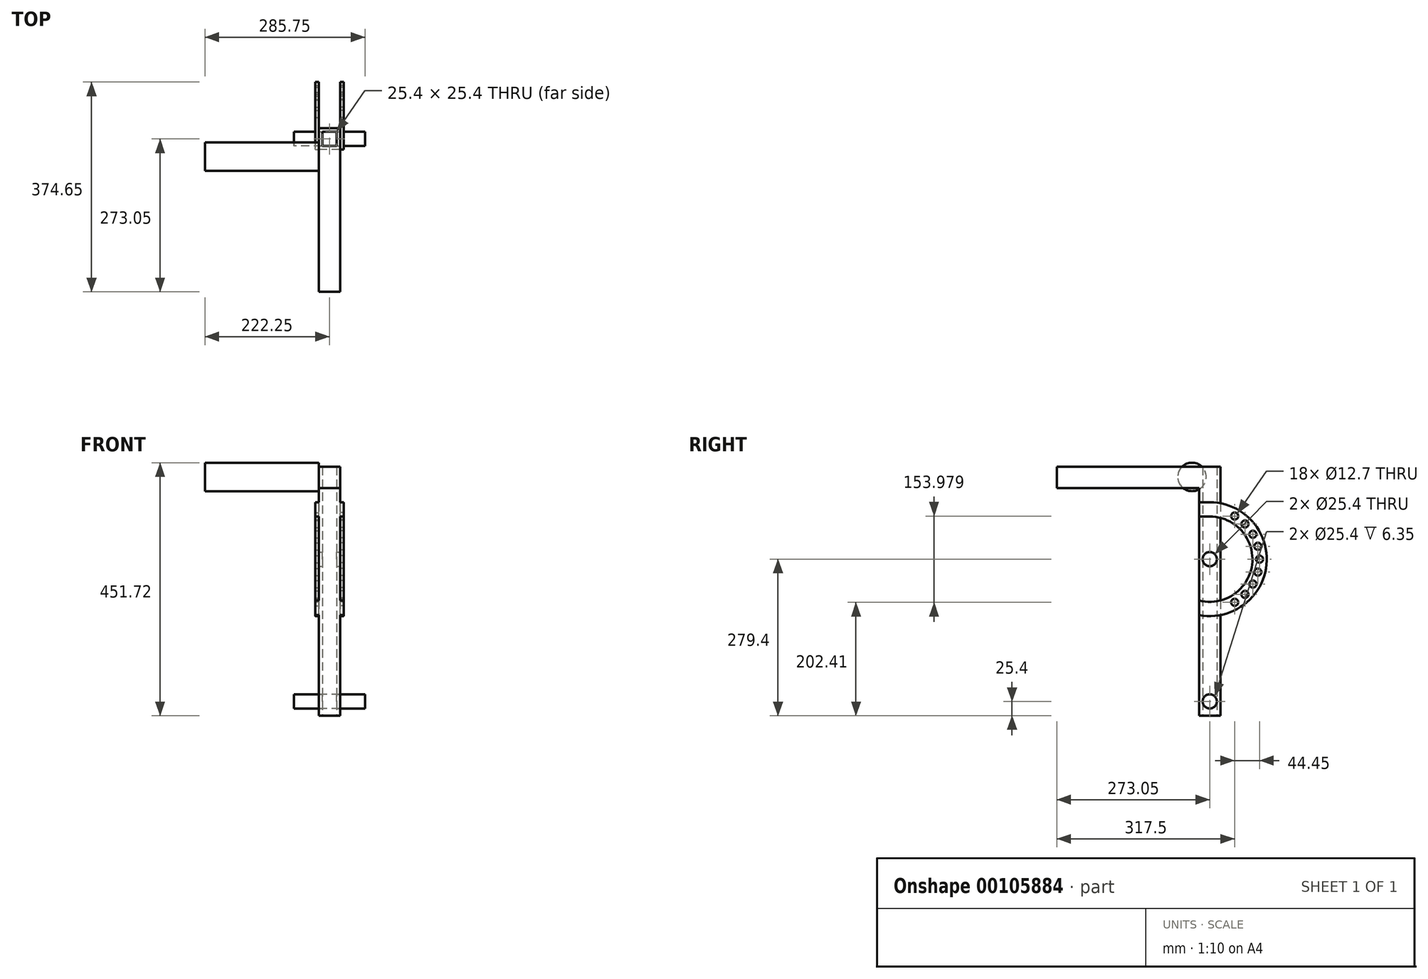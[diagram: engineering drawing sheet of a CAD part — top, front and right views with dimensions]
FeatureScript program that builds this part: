
annotation { "Feature Type Name" : "Feature", "Feature Type Description" : "" }
export const myFeature = defineFeature(function(context is Context, id is Id, definition is map)
    precondition{}
    {
        {
            var Q0;
            Q0=qCreatedBy(makeId("Top.planeOp"),FACE);
            var sketch = newSketch(context, id + "F0", { "sketchPlane" : qUnion([Q0])});
            skLineSegment(sketch, "E0.bottom", {"start": v(19.05, 19.05) * mm, "end": v(-19.05, 19.05) * mm});
            skLineSegment(sketch, "E0.top", {"start": v(19.05, -19.05) * mm, "end": v(-19.05, -19.05) * mm});
            skLineSegment(sketch, "E0.left", {"start": v(19.05, 19.05) * mm, "end": v(19.05, -19.05) * mm});
            skLineSegment(sketch, "E0.right", {"start": v(-19.05, 19.05) * mm, "end": v(-19.05, -19.05) * mm});
            skPoint(sketch, "E0.middle", {"position": v(0, 0) * mm});
            skLineSegment(sketch, "E1.0", {"start": v(12.7, 12.7) * mm, "end": v(-12.7, 12.7) * mm});
            skLineSegment(sketch, "E1.1", {"start": v(12.7, 12.7) * mm, "end": v(12.7, -12.7) * mm});
            skLineSegment(sketch, "E1.2", {"start": v(12.7, -12.7) * mm, "end": v(-12.7, -12.7) * mm});
            skLineSegment(sketch, "E1.3", {"start": v(-12.7, 12.7) * mm, "end": v(-12.7, -12.7) * mm});
            skSolve(sketch);
        }
        {
            var Q0;
            Q0 = qSketchRegion(id + "F0", true);
            extrude(context, id + "F1", {"entities" : qUnion([Q0]), "depth" : 444.5 * mm});
        }
        {
            var Q0;
            Q0=makeQuery(id+"F1.opExtrude","SWEPT_FACE",FACE,{"disambiguationData":[OSD([sQuery(id+"F0.wireOp",EDGE,"E0.left")])]});
            var sketch = newSketch(context, id + "F2", { "sketchPlane" : qUnion([Q0])});
            skCircle(sketch, "E2", {"center": v(0, 25.4) * mm, "radius": 12.7 * mm});
            skLineSegment(sketch, "E3", {"start": v(-19.05, 222.25) * mm, "end": v(19.05, 222.25) * mm, "construction": true});
            skCircle(sketch, "E4", {"center": v(0, 279.4) * mm, "radius": 12.7 * mm});
            skSolve(sketch);
        }
        {
            var Q0;
            Q0 = qSketchRegion(id + "F2", true);
            var Q1;
            Q1=makeQuery(id+"F1.opExtrude","SWEPT_FACE",FACE,{"disambiguationData":[OSD([sQuery(id+"F0.wireOp",EDGE,"E0.right")])]});
            extrude(context, id + "F3", {"entities" : qUnion([Q0]), "operationType" : NewBodyOperationType.REMOVE, "endBound" : BoundingType.UP_TO_SURFACE, "oppositeDirection" : true, "endBoundEntityFace" : qUnion([Q1]), "depth" : 25.4 * mm});
        }
        {
            var Q0;
            Q0=qCreatedBy(makeId("Right.planeOp"),FACE);
            var sketch = newSketch(context, id + "F4", { "sketchPlane" : qUnion([Q0])});
            skCircle(sketch, "E5", {"center": v(0, 25.4) * mm, "radius": 12.7 * mm});
            skSolve(sketch);
        }
        {
            var Q0;
            Q0 = qSketchRegion(id + "F4", true);
            extrude(context, id + "F5", {"entities" : qUnion([Q0]), "endBound" : BoundingType.SYMMETRIC, "depth" : 127 * mm});
        }
        {
            var Q0;
            Q0=makeQuery(id+"F2.imprint","IMPRINT",FACE,{"disambiguationData":[TD([[makeQuery(id+"F2.imprint","IMPRINT",EDGE,{"derivedFrom":sQuery(id+"F2.wireOp",EDGE,"E2")}),-1.0]])]});
            var sketch = newSketch(context, id + "F6", { "sketchPlane" : qUnion([Q0])});
            skArc(sketch, "E6", {"start": v(-19.05, 205.62) * mm, "mid": v(75.6, 269.8) * mm, "end": v(0, 355.6) * mm});
            skArc(sketch, "E7", {"start": v(-19.05, 179.6) * mm, "mid": v(101.15, 269.83) * mm, "end": v(0, 381) * mm});
            skLineSegment(sketch, "E8", {"start": v(-19.05, 179.6) * mm, "end": v(-19.05, 205.62) * mm});
            skLineSegment(sketch, "E9", {"start": v(0, 177.8) * mm, "end": v(0, 381) * mm, "construction": true});
            skLineSegment(sketch, "E10", {"start": v(0, 279.4) * mm, "end": v(26.3, 377.54) * mm, "construction": true});
            skLineSegment(sketch, "E11", {"start": v(0, 279.4) * mm, "end": v(51.4, 368.43) * mm, "construction": true});
            skLineSegment(sketch, "E12", {"start": v(0, 279.4) * mm, "end": v(71.84, 351.24) * mm, "construction": true});
            skLineSegment(sketch, "E13", {"start": v(0, 279.4) * mm, "end": v(87.99, 330.2) * mm, "construction": true});
            skLineSegment(sketch, "E14", {"start": v(0, 279.4) * mm, "end": v(98.14, 305.7) * mm, "construction": true});
            skCircle(sketch, "E15", {"center": v(0, 279.4) * mm, "radius": 88.9 * mm, "construction": true});
            skCircle(sketch, "E16", {"center": v(44.45, 356.39) * mm, "radius": 6.35 * mm});
            skCircle(sketch, "E17", {"center": v(62.86, 342.26) * mm, "radius": 6.35 * mm});
            skCircle(sketch, "E18", {"center": v(76.99, 323.85) * mm, "radius": 6.35 * mm});
            skCircle(sketch, "E19", {"center": v(85.87, 302.4) * mm, "radius": 6.35 * mm});
            skLineSegment(sketch, "E20", {"start": v(-19.05, 381) * mm, "end": v(0, 381) * mm});
            skLineSegment(sketch, "E21", {"start": v(0, 355.6) * mm, "end": v(-19.05, 355.6) * mm});
            skLineSegment(sketch, "E22", {"start": v(-19.05, 355.6) * mm, "end": v(-19.05, 381) * mm});
            skLineSegment(sketch, "E23", {"start": v(0, 279.4) * mm, "end": v(88.9, 279.4) * mm, "construction": true});
            skLineSegment(sketch, "E24", {"start": v(0, 279.4) * mm, "end": v(85.87, 256.4) * mm, "construction": true});
            skLineSegment(sketch, "E25", {"start": v(0, 279.4) * mm, "end": v(76.99, 234.95) * mm, "construction": true});
            skLineSegment(sketch, "E26", {"start": v(0, 279.4) * mm, "end": v(62.86, 216.54) * mm, "construction": true});
            skCircle(sketch, "E27", {"center": v(88.9, 279.4) * mm, "radius": 6.35 * mm});
            skCircle(sketch, "E28", {"center": v(85.87, 256.4) * mm, "radius": 6.35 * mm});
            skCircle(sketch, "E29", {"center": v(76.99, 234.95) * mm, "radius": 6.35 * mm});
            skCircle(sketch, "E30", {"center": v(62.86, 216.54) * mm, "radius": 6.35 * mm});
            skLineSegment(sketch, "E31", {"start": v(0, 279.4) * mm, "end": v(44.45, 202.41) * mm, "construction": true});
            skCircle(sketch, "E32", {"center": v(44.45, 202.41) * mm, "radius": 6.35 * mm});
            skSolve(sketch);
        }
        {
            var Q0;
            Q0 = qSketchRegion(id + "F6", true);
            extrude(context, id + "F7", {"entities" : qUnion([Q0]), "depth" : 6.35 * mm});
        }
        {
            var Q0;
            Q0=makeQuery(id+"F7.opExtrude","SWEPT_BODY",BODY,{"disambiguationData":[OSD([sQuery(id+"F6.wireOp",EDGE,"E6"),sQuery(id+"F6.wireOp",EDGE,"E7"),sQuery(id+"F6.wireOp",EDGE,"E8"),sQuery(id+"F6.wireOp",EDGE,"E16"),sQuery(id+"F6.wireOp",EDGE,"E17"),sQuery(id+"F6.wireOp",EDGE,"E18"),sQuery(id+"F6.wireOp",EDGE,"E19"),sQuery(id+"F6.wireOp",EDGE,"E20"),sQuery(id+"F6.wireOp",EDGE,"E21"),sQuery(id+"F6.wireOp",EDGE,"E22"),sQuery(id+"F6.wireOp",EDGE,"E27"),sQuery(id+"F6.wireOp",EDGE,"E28"),sQuery(id+"F6.wireOp",EDGE,"E29"),sQuery(id+"F6.wireOp",EDGE,"E30"),sQuery(id+"F6.wireOp",EDGE,"E32")])]});
            var Q1;
            Q1=qCreatedBy(makeId("Right.planeOp"),FACE);
            mirror(context, id + "F8", {"operationType" : NewBodyOperationType.ADD, "entities" : qUnion([Q0]), "mirrorPlane" : qUnion([Q1])});
        }
        {
            var Q0;
            {var subQ0=makeQuery(id+"F7.opExtrude","SWEPT_FACE",FACE,{"disambiguationData":[OSD([sQuery(id+"F6.wireOp",EDGE,"E22")])]});var subQ1=makeQuery(id+"F7.opExtrude","SWEPT_FACE",FACE,{"disambiguationData":[OSD([sQuery(id+"F6.wireOp",EDGE,"E8")])]});Q0=makeQuery(id+"F8.boolean.opBoolean","MERGE",FACE,{"derivedFrom":[makeQuery(id+"F1.opExtrude","SWEPT_FACE",FACE,{"disambiguationData":[OSD([sQuery(id+"F0.wireOp",EDGE,"E0.top")])]}),subQ1,subQ0,makeQuery(id+"F8.opPattern","COPY",FACE,{"derivedFrom":subQ1,"instanceName":"1"}),makeQuery(id+"F8.opPattern","COPY",FACE,{"derivedFrom":subQ0,"instanceName":"1"})]});}
            var sketch = newSketch(context, id + "F9", { "sketchPlane" : qUnion([Q0])});
            skLineSegment(sketch, "E33.bottom", {"start": v(19.05, 406.4) * mm, "end": v(-19.05, 406.4) * mm});
            skLineSegment(sketch, "E33.top", {"start": v(19.05, 444.5) * mm, "end": v(-19.05, 444.5) * mm});
            skLineSegment(sketch, "E33.left", {"start": v(19.05, 406.4) * mm, "end": v(19.05, 444.5) * mm});
            skLineSegment(sketch, "E33.right", {"start": v(-19.05, 406.4) * mm, "end": v(-19.05, 444.5) * mm});
            skSolve(sketch);
        }
        {
            var Q0;
            Q0 = qSketchRegion(id + "F9", true);
            extrude(context, id + "F10", {"entities" : qUnion([Q0]), "operationType" : NewBodyOperationType.ADD, "depth" : 254 * mm});
        }
        {
            var Q0;
            Q0=makeQuery(id+"F1.opExtrude","SWEPT_FACE",FACE,{"disambiguationData":[OSD([sQuery(id+"F0.wireOp",EDGE,"E0.right")])]});
            var sketch = newSketch(context, id + "F11", { "sketchPlane" : qUnion([Q0])});
            skCircle(sketch, "E34", {"center": v(31.75, 426.32) * mm, "radius": 25.4 * mm});
            skSolve(sketch);
        }
        {
            var Q0;
            Q0 = qSketchRegion(id + "F11", true);
            extrude(context, id + "F12", {"entities" : qUnion([Q0]), "operationType" : NewBodyOperationType.ADD, "depth" : 203.2 * mm});
        }
    });
